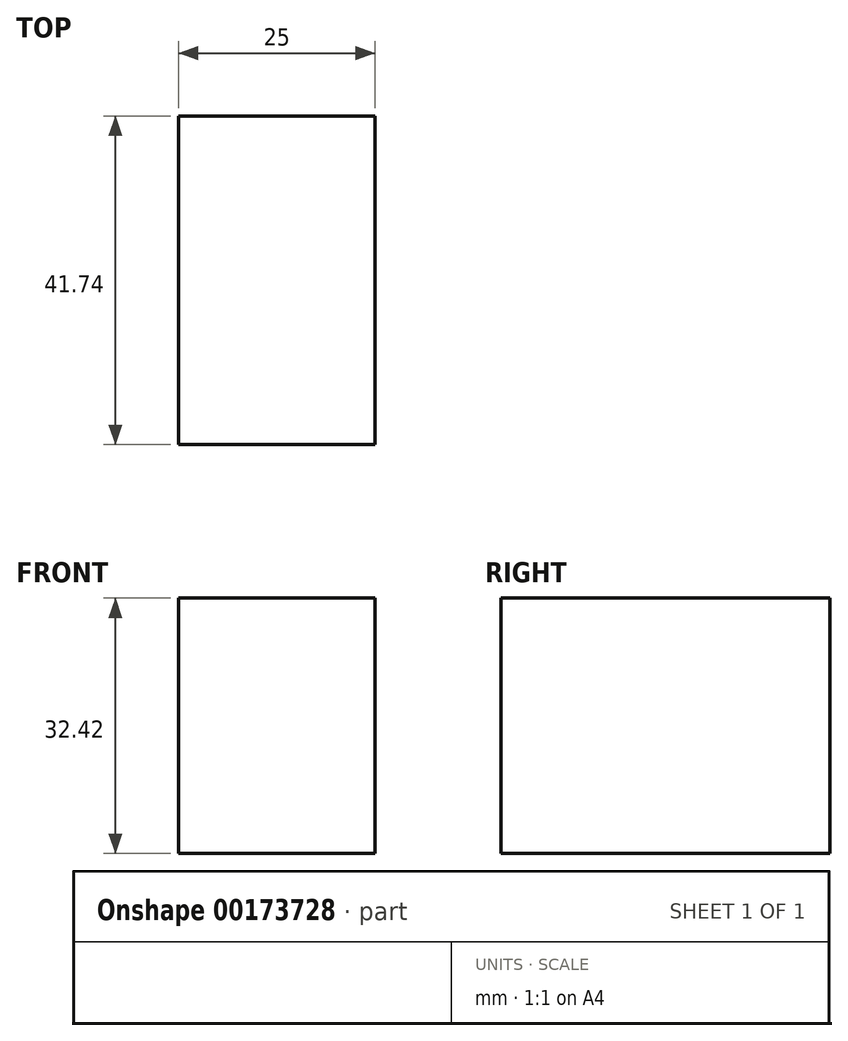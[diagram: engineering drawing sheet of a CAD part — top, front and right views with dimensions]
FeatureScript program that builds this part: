
annotation { "Feature Type Name" : "Feature", "Feature Type Description" : "" }
export const myFeature = defineFeature(function(context is Context, id is Id, definition is map)
    precondition{}
    {
        {
            var Q0;
            Q0=qCreatedBy(makeId("Right.planeOp"),FACE);
            var sketch = newSketch(context, id + "F0", { "sketchPlane" : qUnion([Q0])});
            skLineSegment(sketch, "E0.bottom", {"start": v(41.74, 32.42) * mm, "end": v(0, 32.42) * mm});
            skLineSegment(sketch, "E0.top", {"start": v(41.74, 0) * mm, "end": v(0, 0) * mm});
            skLineSegment(sketch, "E0.left", {"start": v(41.74, 32.42) * mm, "end": v(41.74, 0) * mm});
            skLineSegment(sketch, "E0.right", {"start": v(0, 32.42) * mm, "end": v(0, 0) * mm});
            skSolve(sketch);
        }
        {
            var Q0;
            Q0=makeQuery(id+"F0.imprint","IMPRINT",FACE,{"disambiguationData":[TD([[makeQuery(id+"F0.imprint","IMPRINT",EDGE,{"derivedFrom":sQuery(id+"F0.wireOp",EDGE,"E0.bottom")}),1.0]])]});
            extrude(context, id + "F2", {"entities" : qUnion([Q0]), "depth" : 25 * mm});
        }
    });
